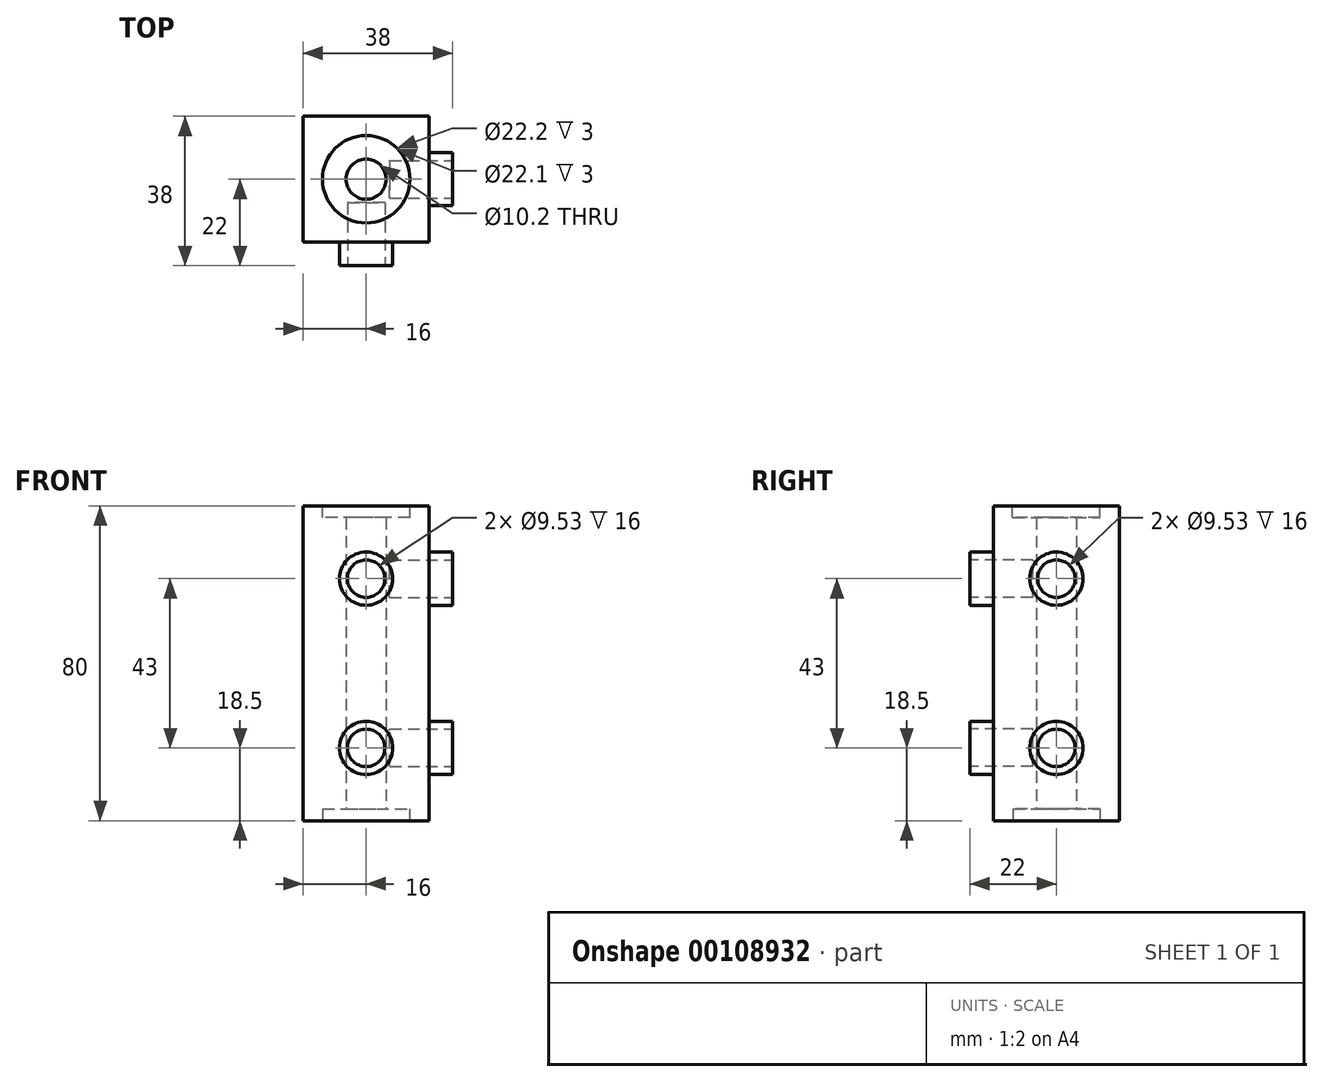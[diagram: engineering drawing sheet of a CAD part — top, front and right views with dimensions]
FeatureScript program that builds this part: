
annotation { "Feature Type Name" : "Feature", "Feature Type Description" : "" }
export const myFeature = defineFeature(function(context is Context, id is Id, definition is map)
    precondition{}
    {
        {
            var Q0;
            Q0=qCreatedBy(makeId("Top.planeOp"),FACE);
            var sketch = newSketch(context, id + "F0", { "sketchPlane" : qUnion([Q0])});
            skLineSegment(sketch, "E0.bottom", {"start": v(16, -16) * mm, "end": v(-16, -16) * mm});
            skLineSegment(sketch, "E0.top", {"start": v(16, 16) * mm, "end": v(-16, 16) * mm});
            skLineSegment(sketch, "E0.left", {"start": v(16, -16) * mm, "end": v(16, 16) * mm});
            skLineSegment(sketch, "E0.right", {"start": v(-16, -16) * mm, "end": v(-16, 16) * mm});
            skPoint(sketch, "E0.middle", {"position": v(0, 0) * mm});
            skSolve(sketch);
        }
        {
            var Q0;
            Q0 = qSketchRegion(id + "F0", true);
            extrude(context, id + "F1", {"entities" : qUnion([Q0]), "endBound" : BoundingType.SYMMETRIC, "depth" : 80 * mm});
        }
        {
            var Q0;
            Q0=makeQuery(id+"F1.opExtrude","SWEPT_FACE",FACE,{"disambiguationData":[OSD([sQuery(id+"F0.wireOp",EDGE,"E0.bottom")])]});
            var sketch = newSketch(context, id + "F2", { "sketchPlane" : qUnion([Q0])});
            skLineSegment(sketch, "E1", {"start": v(0, 0) * mm, "end": v(0, 21.5) * mm, "construction": true});
            skLineSegment(sketch, "E2", {"start": v(0, 0) * mm, "end": v(0, -21.5) * mm, "construction": true});
            skCircle(sketch, "E3", {"center": v(0, 21.5) * mm, "radius": 4.76 * mm});
            skCircle(sketch, "E4", {"center": v(0, -21.5) * mm, "radius": 4.76 * mm});
            skSolve(sketch);
        }
        {
            var Q0;
            Q0 = qSketchRegion(id + "F2", true);
            extrude(context, id + "F3", {"entities" : qUnion([Q0]), "operationType" : NewBodyOperationType.REMOVE, "oppositeDirection" : true, "depth" : 10 * mm});
        }
        {
            var Q0;
            Q0=makeQuery(id+"F1.opExtrude","SWEPT_FACE",FACE,{"disambiguationData":[OSD([sQuery(id+"F0.wireOp",EDGE,"E0.left")])]});
            var sketch = newSketch(context, id + "F4", { "sketchPlane" : qUnion([Q0])});
            skLineSegment(sketch, "E5", {"start": v(0, 0) * mm, "end": v(0, 21.5) * mm, "construction": true});
            skLineSegment(sketch, "E6", {"start": v(0, 0) * mm, "end": v(0, -21.5) * mm, "construction": true});
            skCircle(sketch, "E7", {"center": v(0, 21.5) * mm, "radius": 4.76 * mm});
            skCircle(sketch, "E8", {"center": v(0, -21.5) * mm, "radius": 4.76 * mm});
            skSolve(sketch);
        }
        {
            var Q0;
            Q0 = qSketchRegion(id + "F4", true);
            extrude(context, id + "F5", {"entities" : qUnion([Q0]), "operationType" : NewBodyOperationType.REMOVE, "oppositeDirection" : true, "depth" : 10 * mm});
        }
        {
            var Q0;
            Q0=makeQuery(id+"F1.opExtrude","CAP_FACE",FACE,{"disambiguationData":[OSD([sQuery(id+"F0.wireOp",EDGE,"E0.bottom"),sQuery(id+"F0.wireOp",EDGE,"E0.top"),sQuery(id+"F0.wireOp",EDGE,"E0.left"),sQuery(id+"F0.wireOp",EDGE,"E0.right")])],"isStart":false});
            var sketch = newSketch(context, id + "F6", { "sketchPlane" : qUnion([Q0])});
            skCircle(sketch, "E9", {"center": v(0, 0) * mm, "radius": 11.1 * mm});
            skSolve(sketch);
        }
        {
            var Q0;
            Q0 = qSketchRegion(id + "F6", true);
            extrude(context, id + "F7", {"entities" : qUnion([Q0]), "operationType" : NewBodyOperationType.REMOVE, "oppositeDirection" : true, "depth" : 3 * mm});
        }
        {
            var Q0;
            Q0=makeQuery(id+"F1.opExtrude","CAP_FACE",FACE,{"disambiguationData":[OSD([sQuery(id+"F0.wireOp",EDGE,"E0.bottom"),sQuery(id+"F0.wireOp",EDGE,"E0.top"),sQuery(id+"F0.wireOp",EDGE,"E0.left"),sQuery(id+"F0.wireOp",EDGE,"E0.right")])],"isStart":true});
            var sketch = newSketch(context, id + "F8", { "sketchPlane" : qUnion([Q0])});
            skCircle(sketch, "E10", {"center": v(0, 0) * mm, "radius": 11.05 * mm});
            skSolve(sketch);
        }
        {
            var Q0;
            Q0=makeQuery(id+"F8.imprint","IMPRINT",FACE,{"disambiguationData":[TD([[makeQuery(id+"F8.imprint","IMPRINT",EDGE,{"derivedFrom":sQuery(id+"F8.wireOp",EDGE,"E10")}),1.0]])]});
            extrude(context, id + "F9", {"entities" : qUnion([Q0]), "operationType" : NewBodyOperationType.REMOVE, "oppositeDirection" : true, "depth" : 3 * mm});
        }
        {
            var Q0;
            Q0=makeQuery(id+"F8.imprint","IMPRINT",FACE,{"disambiguationData":[TD([[makeQuery(id+"F8.imprint","IMPRINT",EDGE,{"derivedFrom":sQuery(id+"F8.wireOp",EDGE,"E10")}),1.0]])]});
            var sketch = newSketch(context, id + "F10", { "sketchPlane" : qUnion([Q0])});
            skCircle(sketch, "E11", {"center": v(0, 0) * mm, "radius": 5.1 * mm});
            skSolve(sketch);
        }
        {
            var Q0;
            Q0=makeQuery(id+"F10.imprint","IMPRINT",FACE,{"disambiguationData":[TD([[makeQuery(id+"F10.imprint","IMPRINT",EDGE,{"derivedFrom":sQuery(id+"F10.wireOp",EDGE,"E11")}),1.0]])]});
            extrude(context, id + "F11", {"entities" : qUnion([Q0]), "operationType" : NewBodyOperationType.REMOVE, "endBound" : BoundingType.THROUGH_ALL, "oppositeDirection" : true, "depth" : 25 * mm});
        }
        {
            var Q0;
            Q0=makeQuery(id+"F2.imprint","IMPRINT",FACE,{"disambiguationData":[TD([[makeQuery(id+"F2.imprint","IMPRINT",EDGE,{"derivedFrom":sQuery(id+"F2.wireOp",EDGE,"E3")}),-1.0]])]});
            var sketch = newSketch(context, id + "F12", { "sketchPlane" : qUnion([Q0])});
            skCircle(sketch, "E12.0", {"center": v(0, 21.5) * mm, "radius": 4.76 * mm});
            skCircle(sketch, "E13.0", {"center": v(0, -21.5) * mm, "radius": 4.76 * mm});
            skCircle(sketch, "E14", {"center": v(0, 21.5) * mm, "radius": 6.76 * mm});
            skCircle(sketch, "E15", {"center": v(0, -21.5) * mm, "radius": 6.76 * mm});
            skSolve(sketch);
        }
        {
            var Q0;
            Q0 = qSketchRegion(id + "F12", true);
            extrude(context, id + "F13", {"entities" : qUnion([Q0]), "operationType" : NewBodyOperationType.ADD, "depth" : 6 * mm});
        }
        {
            var Q0;
            Q0=makeQuery(id+"F4.imprint","IMPRINT",FACE,{"disambiguationData":[TD([[makeQuery(id+"F4.imprint","IMPRINT",EDGE,{"derivedFrom":sQuery(id+"F4.wireOp",EDGE,"E7")}),-1.0]])]});
            var sketch = newSketch(context, id + "F14", { "sketchPlane" : qUnion([Q0])});
            skPoint(sketch, "E16.0", {"position": v(0, 21.5) * mm});
            skCircle(sketch, "E17.0", {"center": v(0, 21.5) * mm, "radius": 4.76 * mm});
            skPoint(sketch, "E18.0", {"position": v(0, -21.5) * mm});
            skCircle(sketch, "E19.0", {"center": v(0, -21.5) * mm, "radius": 4.76 * mm});
            skCircle(sketch, "E20", {"center": v(0, 21.5) * mm, "radius": 6.76 * mm});
            skCircle(sketch, "E21", {"center": v(0, -21.5) * mm, "radius": 6.76 * mm});
            skSolve(sketch);
        }
        {
            var Q0;
            Q0 = qSketchRegion(id + "F14", true);
            extrude(context, id + "F15", {"entities" : qUnion([Q0]), "operationType" : NewBodyOperationType.ADD, "depth" : 6 * mm});
        }
    });
